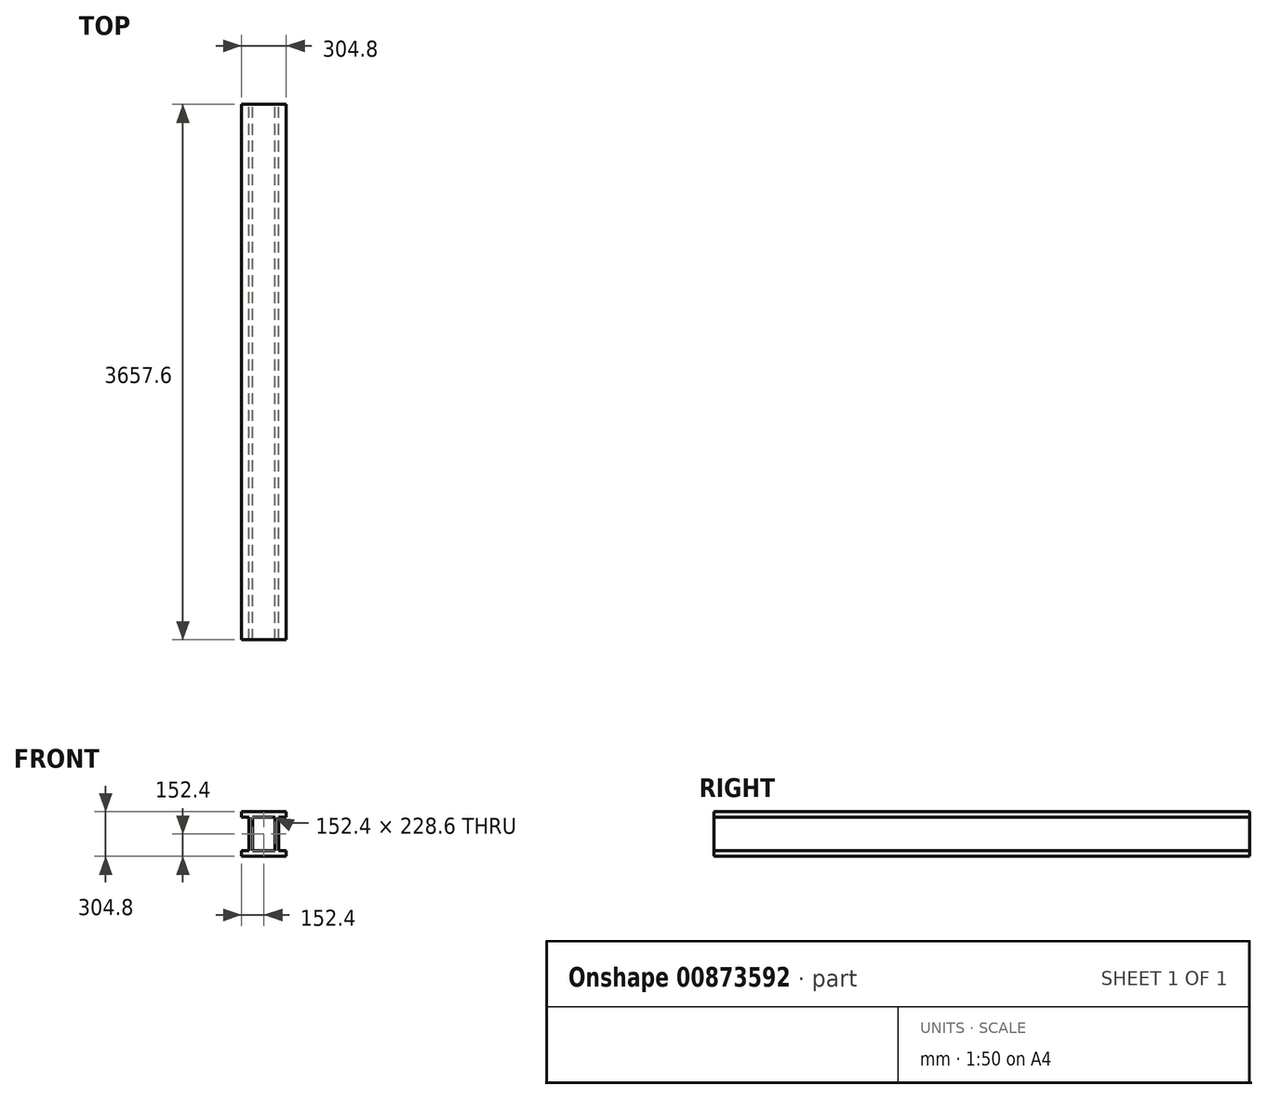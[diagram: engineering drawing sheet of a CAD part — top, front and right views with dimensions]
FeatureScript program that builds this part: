
annotation { "Feature Type Name" : "Feature", "Feature Type Description" : "" }
export const myFeature = defineFeature(function(context is Context, id is Id, definition is map)
    precondition{}
    {
        {
            var Q0;
            Q0=qCreatedBy(makeId("Front.planeOp"),FACE);
            var sketch = newSketch(context, id + "F0", { "sketchPlane" : qUnion([Q0])});
            skLineSegment(sketch, "E0.bottom", {"start": v(0, 0) * mm, "end": v(304.8, 0) * mm});
            skLineSegment(sketch, "E0.top", {"start": v(0, 304.8) * mm, "end": v(304.8, 304.8) * mm});
            skLineSegment(sketch, "E0.left", {"start": v(0, 0) * mm, "end": v(0, 38.1) * mm});
            skLineSegment(sketch, "E0.right", {"start": v(304.8, 0) * mm, "end": v(304.8, 38.1) * mm});
            skLineSegment(sketch, "E1", {"start": v(152.4, 304.8) * mm, "end": v(152.4, -108.56) * mm, "construction": true});
            skLineSegment(sketch, "E2", {"start": v(0, 152.4) * mm, "end": v(388.02, 152.4) * mm, "construction": true});
            skLineSegment(sketch, "E3", {"start": v(0, 266.7) * mm, "end": v(50.8, 266.7) * mm});
            skLineSegment(sketch, "E4", {"start": v(0, 38.1) * mm, "end": v(50.8, 38.1) * mm});
            skLineSegment(sketch, "E5", {"start": v(50.8, 266.7) * mm, "end": v(50.8, 38.1) * mm});
            skLineSegment(sketch, "E6", {"start": v(254, 266.7) * mm, "end": v(254, 38.1) * mm});
            skLineSegment(sketch, "E7", {"start": v(76.2, 266.7) * mm, "end": v(76.2, 38.1) * mm});
            skLineSegment(sketch, "E8", {"start": v(228.6, 266.7) * mm, "end": v(228.6, 38.1) * mm});
            skLineSegment(sketch, "E9.trimOffspring", {"start": v(0, 266.7) * mm, "end": v(0, 304.8) * mm});
            skLineSegment(sketch, "E10.trimOffspring", {"start": v(304.8, 266.7) * mm, "end": v(304.8, 304.8) * mm});
            skLineSegment(sketch, "E11.trimOffspring", {"start": v(76.2, 266.7) * mm, "end": v(228.6, 266.7) * mm});
            skLineSegment(sketch, "E12.trimOffspring", {"start": v(254, 266.7) * mm, "end": v(304.8, 266.7) * mm});
            skLineSegment(sketch, "E13.trimOffspring", {"start": v(76.2, 38.1) * mm, "end": v(228.6, 38.1) * mm});
            skLineSegment(sketch, "E14.trimOffspring", {"start": v(254, 38.1) * mm, "end": v(304.8, 38.1) * mm});
            skLineSegment(sketch, "E15", {"start": v(50.8, 266.7) * mm, "end": v(50.8, 279.4) * mm});
            skLineSegment(sketch, "E16", {"start": v(50.8, 279.4) * mm, "end": v(76.2, 279.4) * mm});
            skLineSegment(sketch, "E17", {"start": v(76.2, 279.4) * mm, "end": v(76.2, 266.7) * mm});
            skLineSegment(sketch, "E18.MirrorCS", {"start": v(254, 266.7) * mm, "end": v(254, 279.4) * mm});
            skLineSegment(sketch, "E19.MirrorCS", {"start": v(254, 279.4) * mm, "end": v(228.6, 279.4) * mm});
            skLineSegment(sketch, "E20.MirrorCS", {"start": v(228.6, 279.4) * mm, "end": v(228.6, 266.7) * mm});
            skLineSegment(sketch, "E21.MirrorCS", {"start": v(50.8, 38.1) * mm, "end": v(50.8, 25.4) * mm});
            skLineSegment(sketch, "E22.MirrorCS", {"start": v(50.8, 25.4) * mm, "end": v(76.2, 25.4) * mm});
            skLineSegment(sketch, "E23.MirrorCS", {"start": v(76.2, 25.4) * mm, "end": v(76.2, 38.1) * mm});
            skLineSegment(sketch, "E24.MirrorCS", {"start": v(228.6, 25.4) * mm, "end": v(228.6, 38.1) * mm});
            skLineSegment(sketch, "E25.MirrorCS", {"start": v(254, 25.4) * mm, "end": v(228.6, 25.4) * mm});
            skLineSegment(sketch, "E26.MirrorCS", {"start": v(254, 38.1) * mm, "end": v(254, 25.4) * mm});
            skSolve(sketch);
        }
        {
            var Q0;
            Q0 = qSketchRegion(id + "F0", true);
            extrude(context, id + "F1", {"entities" : qUnion([Q0]), "depth" : 3657.6 * mm, "offsetDistance" : 25.4 * mm});
        }
    });
